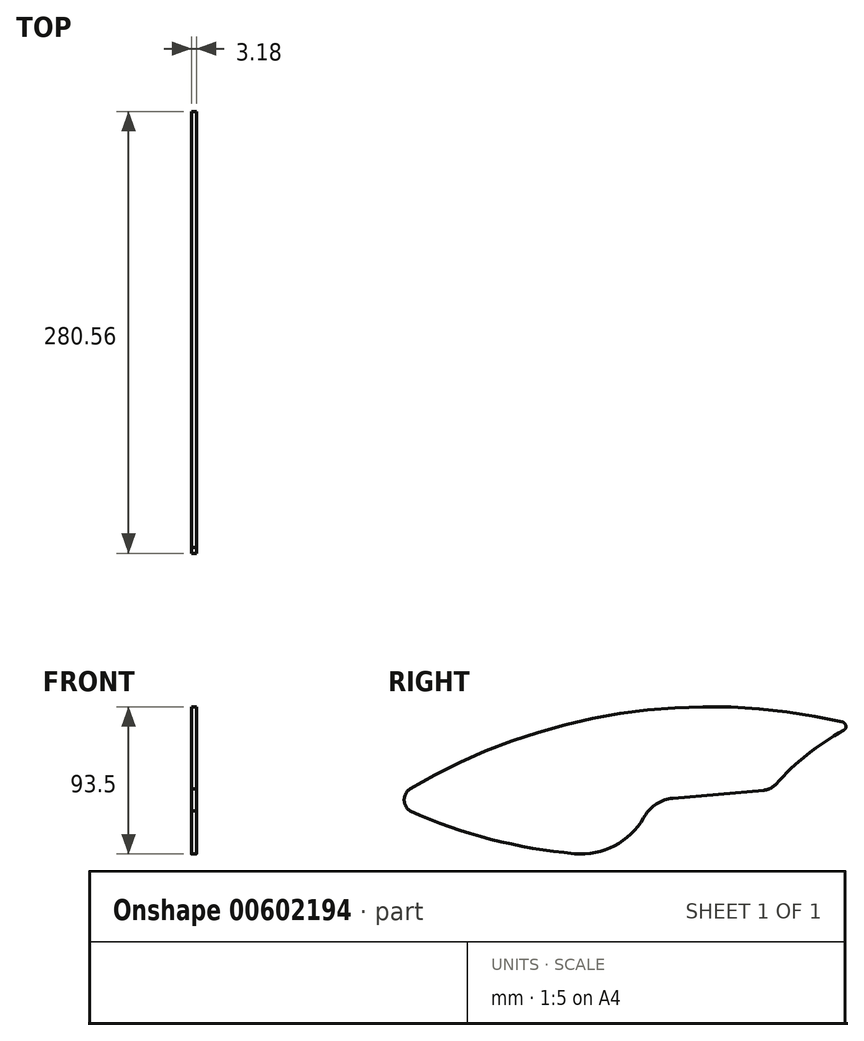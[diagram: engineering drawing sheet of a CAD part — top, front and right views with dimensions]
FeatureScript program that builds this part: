
annotation { "Feature Type Name" : "Feature", "Feature Type Description" : "" }
export const myFeature = defineFeature(function(context is Context, id is Id, definition is map)
    precondition{}
    {
        {
            var Q0;
            Q0=qCreatedBy(makeId("Right.planeOp"),FACE);
            var sketch = newSketch(context, id + "F0", { "sketchPlane" : qUnion([Q0])});
            skArc(sketch, "E0", {"start": v(138.79, 31.7) * mm, "mid": v(140.25, 34.6) * mm, "end": v(138.06, 37) * mm});
            skArc(sketch, "E1", {"start": v(138.06, 37) * mm, "mid": v(-3.33, 42.4) * mm, "end": v(-136.53, -5.33) * mm});
            skArc(sketch, "E2", {"start": v(-136.53, -5.33) * mm, "mid": v(-140.28, -12.43) * mm, "end": v(-136.53, -19.53) * mm});
            skArc(sketch, "E3", {"start": v(-136.53, -19.53) * mm, "mid": v(-85.37, -37.34) * mm, "end": v(-31.99, -46.57) * mm});
            skArc(sketch, "E4", {"start": v(-31.99, -46.57) * mm, "mid": v(-6.76, -41.6) * mm, "end": v(11.83, -23.82) * mm});
            skLineSegment(sketch, "E5", {"start": v(11.83, -23.82) * mm, "end": v(12.45, -22.75) * mm});
            skArc(sketch, "E6", {"start": v(12.45, -22.75) * mm, "mid": v(19.97, -14.88) * mm, "end": v(30.27, -11.37) * mm});
            skLineSegment(sketch, "E7", {"start": v(30.27, -11.37) * mm, "end": v(88.24, -6.21) * mm});
            skArc(sketch, "E8", {"start": v(88.24, -6.21) * mm, "mid": v(92.36, -5.04) * mm, "end": v(95.76, -2.44) * mm});
            skArc(sketch, "E9", {"start": v(95.76, -2.44) * mm, "mid": v(115.82, 16.46) * mm, "end": v(138.79, 31.7) * mm});
            skSolve(sketch);
        }
        {
            var Q0;
            Q0 = qSketchRegion(id + "F0", true);
            extrude(context, id + "F1", {"entities" : qUnion([Q0]), "depth" : 3.17 * mm, "offsetDistance" : 25.4 * mm});
        }
    });
